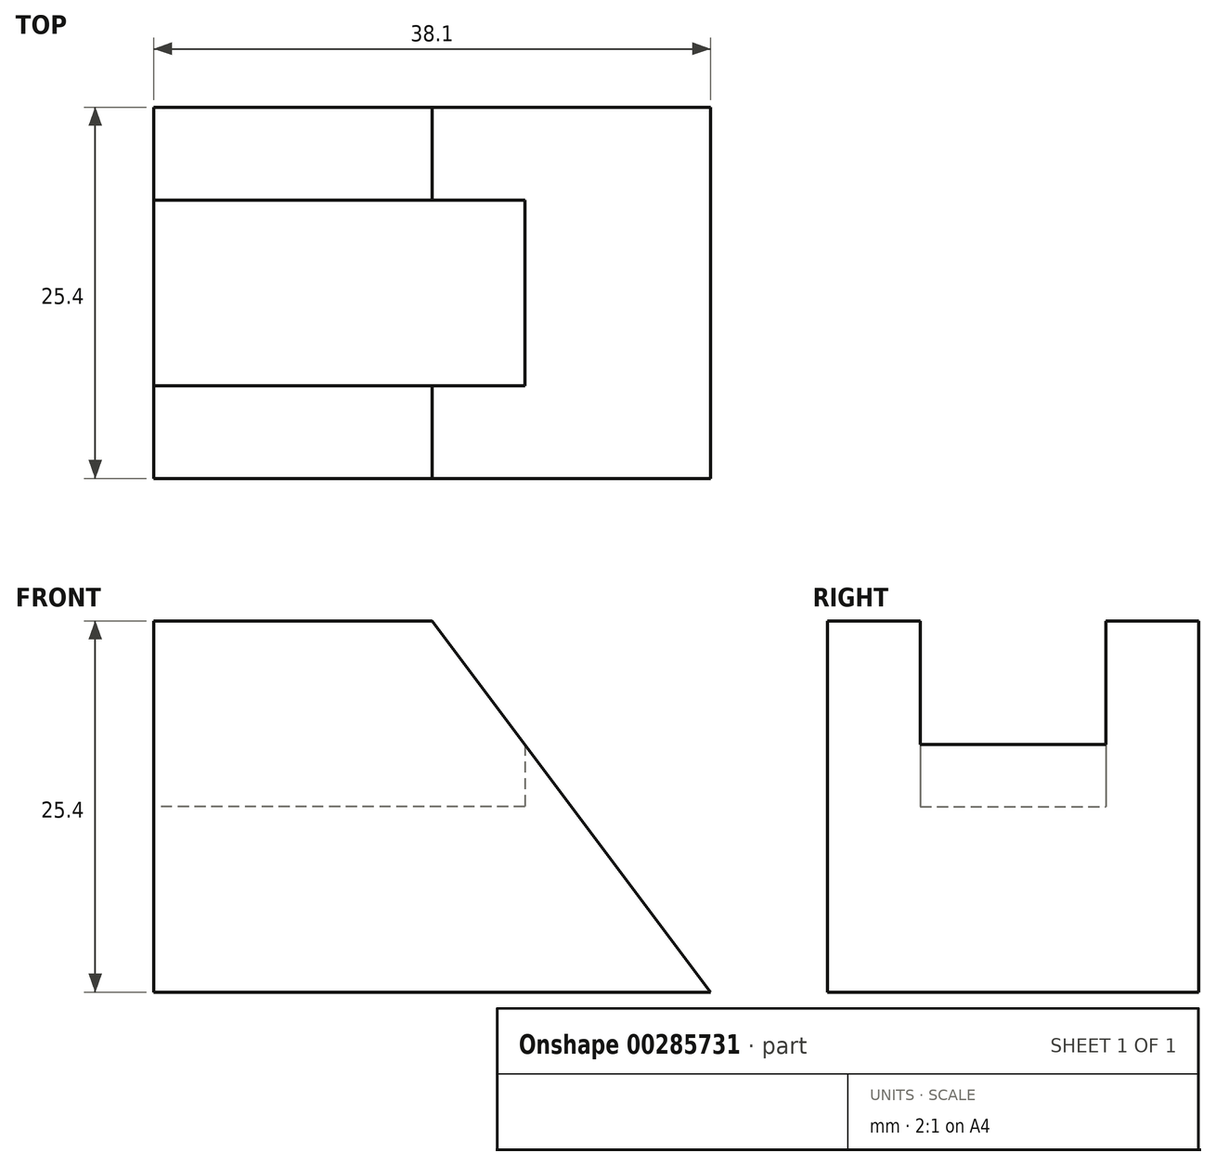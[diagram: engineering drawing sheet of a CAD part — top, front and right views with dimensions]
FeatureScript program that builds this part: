
annotation { "Feature Type Name" : "Feature", "Feature Type Description" : "" }
export const myFeature = defineFeature(function(context is Context, id is Id, definition is map)
    precondition{}
    {
        {
            var Q0;
            Q0=qCreatedBy(makeId("Front.planeOp"),FACE);
            var sketch = newSketch(context, id + "F0", { "sketchPlane" : qUnion([Q0])});
            skLineSegment(sketch, "E0", {"start": v(0, 0) * mm, "end": v(0, 25.4) * mm});
            skLineSegment(sketch, "E1", {"start": v(0, 25.4) * mm, "end": v(19.05, 25.4) * mm});
            skLineSegment(sketch, "E2", {"start": v(19.05, 25.4) * mm, "end": v(38.1, 0) * mm});
            skLineSegment(sketch, "E3", {"start": v(38.1, 0) * mm, "end": v(0, 0) * mm});
            skSolve(sketch);
        }
        {
            var Q0;
            Q0 = qSketchRegion(id + "F0", true);
            extrude(context, id + "F1", {"entities" : qUnion([Q0]), "oppositeDirection" : true, "depth" : 25.4 * mm});
        }
        {
            var Q0;
            Q0=qCreatedBy(makeId("Right.planeOp"),FACE);
            var sketch = newSketch(context, id + "F2", { "sketchPlane" : qUnion([Q0])});
            skLineSegment(sketch, "E4", {"start": v(6.35, 25.4) * mm, "end": v(6.35, 12.7) * mm});
            skLineSegment(sketch, "E5", {"start": v(19.05, 25.4) * mm, "end": v(19.05, 12.7) * mm});
            skLineSegment(sketch, "E6", {"start": v(6.35, 12.7) * mm, "end": v(19.05, 12.7) * mm});
            skLineSegment(sketch, "E7", {"start": v(6.35, 25.4) * mm, "end": v(19.05, 25.4) * mm});
            skSolve(sketch);
        }
        {
            var Q0;
            Q0 = qSketchRegion(id + "F2", true);
            extrude(context, id + "F3", {"entities" : qUnion([Q0]), "operationType" : NewBodyOperationType.REMOVE, "depth" : 25.4 * mm});
        }
    });
